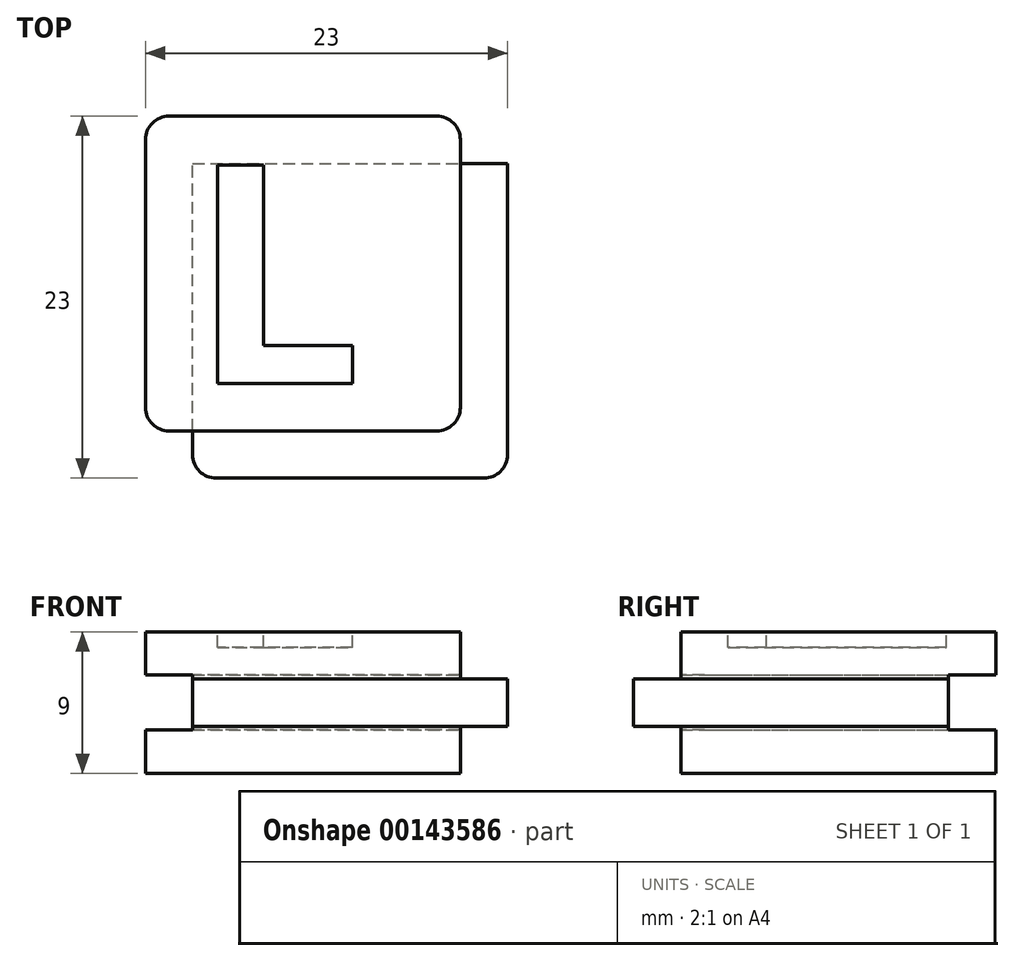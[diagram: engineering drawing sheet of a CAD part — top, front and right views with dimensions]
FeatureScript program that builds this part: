
annotation { "Feature Type Name" : "Feature", "Feature Type Description" : "" }
export const myFeature = defineFeature(function(context is Context, id is Id, definition is map)
    precondition{}
    {
        {
            var Q0;
            Q0=qCreatedBy(makeId("Front.planeOp"),FACE);
            var sketch = newSketch(context, id + "F0", { "sketchPlane" : qUnion([Q0])});
            skLineSegment(sketch, "E0.bottom", {"start": v(10, 4.5) * mm, "end": v(-10, 4.5) * mm});
            skLineSegment(sketch, "E0.top", {"start": v(10, -4.5) * mm, "end": v(-10, -4.5) * mm});
            skLineSegment(sketch, "E0.left", {"start": v(10, 4.5) * mm, "end": v(10, -4.5) * mm});
            skLineSegment(sketch, "E0.right", {"start": v(-10, 4.5) * mm, "end": v(-10, -4.5) * mm});
            skPoint(sketch, "E0.middle", {"position": v(0, 0) * mm});
            skLineSegment(sketch, "E1.bottom", {"start": v(13, 1.5) * mm, "end": v(7, 1.5) * mm});
            skLineSegment(sketch, "E1.top", {"start": v(13, -1.5) * mm, "end": v(7, -1.5) * mm});
            skLineSegment(sketch, "E1.left", {"start": v(13, 1.5) * mm, "end": v(13, -1.5) * mm});
            skLineSegment(sketch, "E1.right", {"start": v(7, 1.5) * mm, "end": v(7, -1.5) * mm});
            skPoint(sketch, "E1.middle", {"position": v(10, 0) * mm});
            skLineSegment(sketch, "E2.bottom", {"start": v(7, 1.5) * mm, "end": v(-7, 1.5) * mm});
            skLineSegment(sketch, "E2.top", {"start": v(7, -1.5) * mm, "end": v(-7, -1.5) * mm});
            skLineSegment(sketch, "E2.right", {"start": v(-7, 1.5) * mm, "end": v(-7, -1.5) * mm});
            skLineSegment(sketch, "E3.bottom", {"start": v(-7, -1.5) * mm, "end": v(-10, -1.5) * mm});
            skLineSegment(sketch, "E3.top", {"start": v(-7, 1.5) * mm, "end": v(-10, 1.5) * mm});
            skLineSegment(sketch, "E3.left", {"start": v(-7, -1.5) * mm, "end": v(-7, 1.5) * mm});
            skLineSegment(sketch, "E3.right", {"start": v(-10, -1.5) * mm, "end": v(-10, 1.5) * mm});
            skSolve(sketch);
        }
        {
            var Q0;
            {var subQ5=sQuery(id+"F0.wireOp",EDGE,"E0.bottom");Q0=makeQuery(id+"F0.imprint","IMPRINT",FACE,{"disambiguationData":[TD([[makeQuery(id+"F0.imprint","IMPRINT",EDGE,{"derivedFrom":subQ5}),1.0]])]});}
            var Q1;
            Q1=makeQuery(id+"F0.imprint","IMPRINT",FACE,{"disambiguationData":[TD([[makeQuery(id+"F0.imprint","IMPRINT",EDGE,{"derivedFrom":sQuery(id+"F0.wireOp",EDGE,"E2.bottom")}),1.0]])]});
            var Q2;
            {var subQ5=sQuery(id+"F0.wireOp",EDGE,"E1.left");Q2=makeQuery(id+"F0.imprint","IMPRINT",FACE,{"disambiguationData":[TD([[makeQuery(id+"F0.imprint","IMPRINT",EDGE,{"derivedFrom":subQ5}),-1.0]])]});}
            var Q3;
            {var subQ5=sQuery(id+"F0.wireOp",EDGE,"E1.right");Q3=makeQuery(id+"F0.imprint","IMPRINT",FACE,{"disambiguationData":[TD([[makeQuery(id+"F0.imprint","IMPRINT",EDGE,{"derivedFrom":subQ5}),1.0]])]});}
            var Q4;
            Q4=makeQuery(id+"F0.imprint","IMPRINT",FACE,{"disambiguationData":[TD([[makeQuery(id+"F0.imprint","IMPRINT",EDGE,{"derivedFrom":sQuery(id+"F0.wireOp",EDGE,"E3.bottom")}),-1.0]])]});
            var Q5;
            {var subQ5=sQuery(id+"F0.wireOp",EDGE,"E0.top");Q5=makeQuery(id+"F0.imprint","IMPRINT",FACE,{"disambiguationData":[TD([[makeQuery(id+"F0.imprint","IMPRINT",EDGE,{"derivedFrom":subQ5}),-1.0]])]});}
            extrude(context, id + "F1", {"entities" : qUnion([Q0, Q1, Q2, Q3, Q4, Q5]), "oppositeDirection" : true, "depth" : 20 * mm});
        }
        {
            var Q0;
            Q0=makeQuery(id+"F0.imprint","IMPRINT",FACE,{"disambiguationData":[TD([[makeQuery(id+"F0.imprint","IMPRINT",EDGE,{"derivedFrom":sQuery(id+"F0.wireOp",EDGE,"E3.bottom")}),-1.0]])]});
            var Q1;
            Q1=makeQuery(id+"F0.imprint","IMPRINT",FACE,{"disambiguationData":[TD([[makeQuery(id+"F0.imprint","IMPRINT",EDGE,{"derivedFrom":sQuery(id+"F0.wireOp",EDGE,"E2.bottom")}),1.0]])]});
            var Q2;
            {var subQ5=sQuery(id+"F0.wireOp",EDGE,"E1.right");Q2=makeQuery(id+"F0.imprint","IMPRINT",FACE,{"disambiguationData":[TD([[makeQuery(id+"F0.imprint","IMPRINT",EDGE,{"derivedFrom":subQ5}),1.0]])]});}
            var Q3;
            {var subQ5=sQuery(id+"F0.wireOp",EDGE,"E1.left");Q3=makeQuery(id+"F0.imprint","IMPRINT",FACE,{"disambiguationData":[TD([[makeQuery(id+"F0.imprint","IMPRINT",EDGE,{"derivedFrom":subQ5}),-1.0]])]});}
            extrude(context, id + "F2", {"entities" : qUnion([Q0, Q1, Q2, Q3]), "operationType" : NewBodyOperationType.ADD, "depth" : 3 * mm});
        }
        {
            var Q0;
            {var subQ0=sQuery(id+"F0.wireOp",EDGE,"E1.left");Q0=makeQuery(id+"F2.boolean.opBoolean","MERGE",FACE,{"derivedFrom":[makeQuery(id+"F1.opExtrude","SWEPT_FACE",FACE,{"disambiguationData":[OSD([subQ0])]}),makeQuery(id+"F2.opExtrude","SWEPT_FACE",FACE,{"disambiguationData":[OSD([subQ0])]})]});}
            var sketch = newSketch(context, id + "F3", { "sketchPlane" : qUnion([Q0])});
            skLineSegment(sketch, "E4.bottom", {"start": v(23, 1.75) * mm, "end": v(17, 1.75) * mm});
            skLineSegment(sketch, "E4.top", {"start": v(23, -1.75) * mm, "end": v(17, -1.75) * mm});
            skLineSegment(sketch, "E4.left", {"start": v(23, 1.75) * mm, "end": v(23, -1.75) * mm});
            skLineSegment(sketch, "E4.right", {"start": v(17, 1.75) * mm, "end": v(17, -1.75) * mm});
            skPoint(sketch, "E4.middle", {"position": v(20, 0) * mm});
            skSolve(sketch);
        }
        {
            var Q0;
            {var subQ1=sQuery(id+"F3.wireOp",EDGE,"E4.bottom");Q0=makeQuery(id+"F3.imprint","IMPRINT",FACE,{"disambiguationData":[TD([[makeQuery(id+"F3.imprint","IMPRINT",EDGE,{"derivedFrom":subQ1}),1.0]])]});}
            var Q1;
            {var subQ1=sQuery(id+"F0.wireOp",EDGE,"E1.left");var subQ8=makeQuery(id+"F1.opExtrude","CAP_EDGE",EDGE,{"disambiguationData":[OSD([subQ1])],"isStart":false});Q1=makeQuery(id+"F3.imprint","IMPRINT",FACE,{"disambiguationData":[TD([[makeQuery(id+"F3.imprint","IMPRINT",EDGE,{"derivedFrom":subQ8}),-1.0]])]});}
            extrude(context, id + "F4", {"entities" : qUnion([Q0, Q1]), "operationType" : NewBodyOperationType.REMOVE, "oppositeDirection" : true, "depth" : 100 * mm});
        }
        {
            var Q0;
            Q0=makeQuery(id+"F4.boolean.opBoolean","COPY",FACE,{"derivedFrom":makeQuery(id+"F4.opExtrude","SWEPT_FACE",FACE,{"disambiguationData":[OSD([sQuery(id+"F3.wireOp",EDGE,"E4.right")])]})});
            var sketch = newSketch(context, id + "F5", { "sketchPlane" : qUnion([Q0])});
            skLineSegment(sketch, "E5.bottom", {"start": v(13, 1.75) * mm, "end": v(7, 1.75) * mm});
            skLineSegment(sketch, "E5.top", {"start": v(13, -1.75) * mm, "end": v(7, -1.75) * mm});
            skLineSegment(sketch, "E5.left", {"start": v(13, 1.75) * mm, "end": v(13, -1.75) * mm});
            skLineSegment(sketch, "E5.right", {"start": v(7, 1.75) * mm, "end": v(7, -1.75) * mm});
            skPoint(sketch, "E5.middle", {"position": v(10, 0) * mm});
            skSolve(sketch);
        }
        {
            var Q0;
            {var subQ3=sQuery(id+"F5.wireOp",EDGE,"E5.left");Q0=makeQuery(id+"F5.imprint","IMPRINT",FACE,{"disambiguationData":[TD([[makeQuery(id+"F5.imprint","IMPRINT",EDGE,{"derivedFrom":subQ3}),-1.0]])]});}
            var Q1;
            {var subQ4=sQuery(id+"F5.wireOp",EDGE,"E5.right");Q1=makeQuery(id+"F5.imprint","IMPRINT",FACE,{"disambiguationData":[TD([[makeQuery(id+"F5.imprint","IMPRINT",EDGE,{"derivedFrom":subQ4}),1.0]])]});}
            extrude(context, id + "F6", {"entities" : qUnion([Q0, Q1]), "operationType" : NewBodyOperationType.REMOVE, "oppositeDirection" : true, "depth" : 100 * mm});
        }
        {
            var Q0;
            Q0=makeQuery(id+"F6.boolean.opBoolean","INTERSECT",EDGE,{"derivedFrom":[makeQuery(id+"F2.opExtrude","CAP_FACE",FACE,{"disambiguationData":[OSD([sQuery(id+"F0.wireOp",EDGE,"E1.bottom"),sQuery(id+"F0.wireOp",EDGE,"E1.top"),sQuery(id+"F0.wireOp",EDGE,"E1.left"),sQuery(id+"F0.wireOp",EDGE,"E2.bottom"),sQuery(id+"F0.wireOp",EDGE,"E2.top"),sQuery(id+"F0.wireOp",EDGE,"E3.bottom"),sQuery(id+"F0.wireOp",EDGE,"E3.top"),sQuery(id+"F0.wireOp",EDGE,"E3.right")])],"isStart":false}),makeQuery(id+"F6.opExtrude","SWEPT_FACE",FACE,{"disambiguationData":[OSD([sQuery(id+"F5.wireOp",EDGE,"E5.right")])]})]});
            var Q1;
            Q1=makeQuery(id+"F2.opExtrude","CAP_EDGE",EDGE,{"disambiguationData":[OSD([sQuery(id+"F0.wireOp",EDGE,"E1.left")])],"isStart":false});
            var Q2;
            {var subQ0=sQuery(id+"F0.wireOp",EDGE,"E0.left");Q2=makeQuery(id+"F1.opExtrude","CAP_EDGE",EDGE,{"disambiguationData":[OSD([subQ0]),TDD([makeQuery(id+"F0.imprint","IMPRINT",EDGE,{"disambiguationData":[TD([[makeQuery(id+"F0.imprint","INTERSECT",VERTEX,{"derivedFrom":[sQuery(id+"F0.wireOp",EDGE,"E0.bottom"),subQ0]}),-1.0]])],"derivedFrom":subQ0})])],"isStart":true});}
            var Q3;
            {var subQ0=sQuery(id+"F0.wireOp",EDGE,"E0.left");Q3=makeQuery(id+"F1.opExtrude","CAP_EDGE",EDGE,{"disambiguationData":[OSD([subQ0]),TDD([makeQuery(id+"F0.imprint","IMPRINT",EDGE,{"disambiguationData":[TD([[makeQuery(id+"F0.imprint","INTERSECT",VERTEX,{"derivedFrom":[sQuery(id+"F0.wireOp",EDGE,"E0.top"),subQ0]}),1.0]])],"derivedFrom":subQ0})])],"isStart":true});}
            var Q4;
            {var subQ0=sQuery(id+"F0.wireOp",EDGE,"E3.right");var subQ1=sQuery(id+"F0.wireOp",EDGE,"E0.right");var subQ3=sQuery(id+"F0.wireOp",EDGE,"E0.top");Q4=makeQuery(id+"F2.boolean.opBoolean","SPLIT",EDGE,{"disambiguationData":[TD([makeQuery(id+"F1.opExtrude","SWEPT_FACE",FACE,{"disambiguationData":[OSD([subQ3])]})])],"derivedFrom":makeQuery(id+"F1.opExtrude","CAP_EDGE",EDGE,{"disambiguationData":[OSD([subQ1,subQ0])],"isStart":true})});}
            var Q5;
            {var subQ1=sQuery(id+"F0.wireOp",EDGE,"E3.right");var subQ2=sQuery(id+"F0.wireOp",EDGE,"E0.right");var subQ3=sQuery(id+"F0.wireOp",EDGE,"E0.bottom");Q5=makeQuery(id+"F2.boolean.opBoolean","SPLIT",EDGE,{"disambiguationData":[TD([makeQuery(id+"F1.opExtrude","SWEPT_FACE",FACE,{"disambiguationData":[OSD([subQ3])]})])],"derivedFrom":makeQuery(id+"F1.opExtrude","CAP_EDGE",EDGE,{"disambiguationData":[OSD([subQ2,subQ1])],"isStart":true})});}
            var Q6;
            Q6=makeQuery(id+"F6.boolean.opBoolean","COPY",EDGE,{"derivedFrom":makeQuery(id+"F6.opExtrude","CAP_EDGE",EDGE,{"disambiguationData":[OSD([sQuery(id+"F5.wireOp",EDGE,"E5.right")])],"isStart":true})});
            var Q7;
            {var subQ0=sQuery(id+"F0.wireOp",EDGE,"E3.right");var subQ1=sQuery(id+"F0.wireOp",EDGE,"E0.right");var subQ2=sQuery(id+"F0.wireOp",EDGE,"E0.bottom");Q7=makeQuery(id+"F4.boolean.opBoolean","SPLIT",EDGE,{"disambiguationData":[TD([makeQuery(id+"F1.opExtrude","SWEPT_FACE",FACE,{"disambiguationData":[OSD([subQ2])]})])],"derivedFrom":makeQuery(id+"F1.opExtrude","CAP_EDGE",EDGE,{"disambiguationData":[OSD([subQ1,subQ0])],"isStart":false})});}
            var Q8;
            {var subQ0=sQuery(id+"F0.wireOp",EDGE,"E3.right");var subQ1=sQuery(id+"F0.wireOp",EDGE,"E0.right");var subQ2=sQuery(id+"F0.wireOp",EDGE,"E0.top");Q8=makeQuery(id+"F4.boolean.opBoolean","SPLIT",EDGE,{"disambiguationData":[TD([makeQuery(id+"F1.opExtrude","SWEPT_FACE",FACE,{"disambiguationData":[OSD([subQ2])]})])],"derivedFrom":makeQuery(id+"F1.opExtrude","CAP_EDGE",EDGE,{"disambiguationData":[OSD([subQ1,subQ0])],"isStart":false})});}
            var Q9;
            Q9=makeQuery(id+"F4.boolean.opBoolean","COPY",EDGE,{"derivedFrom":makeQuery(id+"F4.opExtrude","CAP_EDGE",EDGE,{"disambiguationData":[OSD([sQuery(id+"F3.wireOp",EDGE,"E4.right")])],"isStart":true})});
            var Q10;
            {var subQ0=sQuery(id+"F0.wireOp",EDGE,"E0.left");Q10=makeQuery(id+"F1.opExtrude","CAP_EDGE",EDGE,{"disambiguationData":[OSD([subQ0]),TDD([makeQuery(id+"F0.imprint","IMPRINT",EDGE,{"disambiguationData":[TD([[makeQuery(id+"F0.imprint","INTERSECT",VERTEX,{"derivedFrom":[sQuery(id+"F0.wireOp",EDGE,"E0.bottom"),subQ0]}),-1.0]])],"derivedFrom":subQ0})])],"isStart":false});}
            var Q11;
            {var subQ0=sQuery(id+"F0.wireOp",EDGE,"E0.left");Q11=makeQuery(id+"F1.opExtrude","CAP_EDGE",EDGE,{"disambiguationData":[OSD([subQ0]),TDD([makeQuery(id+"F0.imprint","IMPRINT",EDGE,{"disambiguationData":[TD([[makeQuery(id+"F0.imprint","INTERSECT",VERTEX,{"derivedFrom":[sQuery(id+"F0.wireOp",EDGE,"E0.top"),subQ0]}),1.0]])],"derivedFrom":subQ0})])],"isStart":false});}
            fillet(context, id + "F7", {"entities" : qUnion([Q0, Q1, Q2, Q3, Q4, Q5, Q6, Q7, Q8, Q9, Q10, Q11]), "radius" : 1.5 * mm, "tangentPropagation" : true, "allowEdgeOverflow" : false});
        }
        {
            var Q0;
            Q0=makeQuery(id+"F1.opExtrude","SWEPT_FACE",FACE,{"disambiguationData":[OSD([sQuery(id+"F0.wireOp",EDGE,"E0.bottom")])]});
            var sketch = newSketch(context, id + "F8", { "sketchPlane" : qUnion([Q0])});
            skText(sketch, "E6", { "text": "L", "fontName": "OpenSans-Bold.ttf"});
            skLineSegment(sketch, "E7.0", {"start": v(8.29, 3) * mm, "end": v(-11.07, 3) * mm});
            const initialGuessF8  = {"E6": [-0.00718, 0.003, 1, 0, 0.014]};
            skSetInitialGuess(sketch, initialGuessF8);
            skSolve(sketch);
        }
        {
            var Q0;
            {var subQ0=sQuery(id+"F8.wireOp",EDGE,"E6.sketch_text.stroke-1");Q0=makeQuery(id+"F8.imprint","IMPRINT",FACE,{"disambiguationData":[TD([[makeQuery(id+"F8.imprint","IMPRINT",EDGE,{"derivedFrom":subQ0}),-1.0]])]});}
            extrude(context, id + "F9", {"entities" : qUnion([Q0]), "operationType" : NewBodyOperationType.REMOVE, "oppositeDirection" : true, "depth" : 1 * mm});
        }
    });
